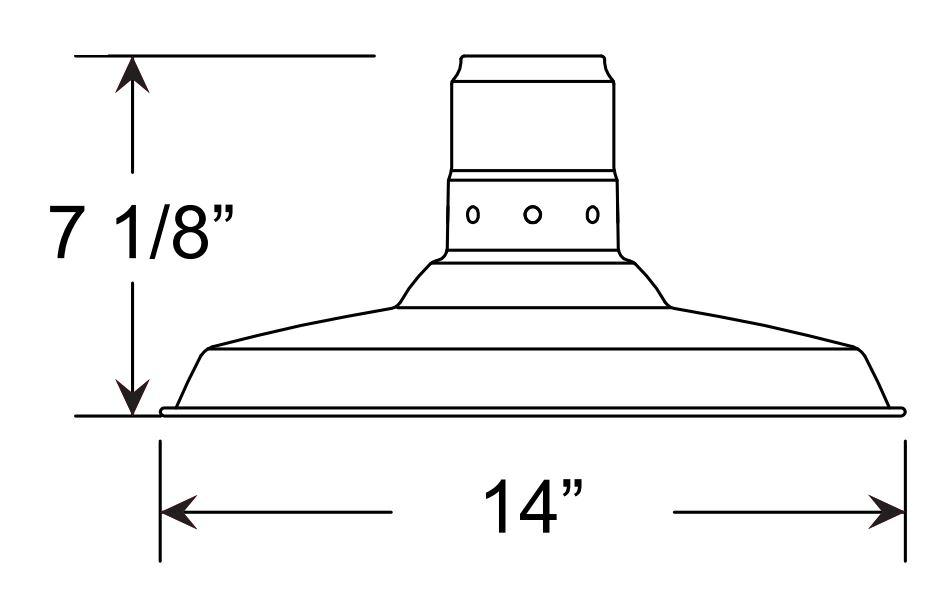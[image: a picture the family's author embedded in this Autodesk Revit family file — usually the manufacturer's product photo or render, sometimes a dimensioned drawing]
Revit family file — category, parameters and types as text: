
# Revit family: OSDD_MB 22,30,36
name_source: partatom
category: Lighting Fixtures
units: mm (PartAtom-declared; Revit-internal decimal feet)

## family parameters
Always vertical = Yes
Cut with Voids When Loaded = No
Light Source = Yes
OmniClass Number = 23.80.70.00
OmniClass Title = Lighting
Part Type = Normal
Room Calculation Point = No
Round Connector Dimension = Use Diameter
Shared = No
Work Plane-Based = No

## types (3) — shared parameters
Apparent Load = 200 VA
Body Colour = Spun aluminium
Body Material = body
Bulb = BULB
CRI = >90
Color Filter = 16777215
Construction Material = Heavy Duty spun aluminum.
Default Elevation = 0' - 0"
Description = 120-277 Voltage
Dimming = 1%
Dimming Lamp Color Temperature Shift = <None>
Efficiency = 65-125 lumens per watt
GLASS = Glass
Inside body material = INSIDE BODY MATERIAL
Lamp = 200W MAX MEDIUM BASE
Life = L70 50,000 hours
Load Classification = Lighting
Manufacturer = ANP Lighting
Photometric Web File = OSDD30M037LDDW35K.ies
Power Factor = 1
Tilt Angle = 90.00°
URL = https://www.anplighting.com
Voltage = 120 V
Warranty = 5 year limited warranty
Wattage Comments = 200W

## per-type parameters (varying)
| type | Fixture Diameter | Fixture Height | OSDD22 | OSDD30 | OSDD36 | Weight |
| OSDD22 | 1' - 10" | 1' - 1" | Yes | No | No | 13.0 lb |
| OSDD30 | 2' - 6" | 1' - 7" | No | Yes | No | 15.0 lb |
| OSDD36 | 3' - 0" | 1' - 9" | No | No | Yes | 18.0 lb |

note: column(s) folded — value = type name in every type: Model

## geometry (parser evidence)
native form markers: Sweep x51
no freeform markers — native parametric forms only
